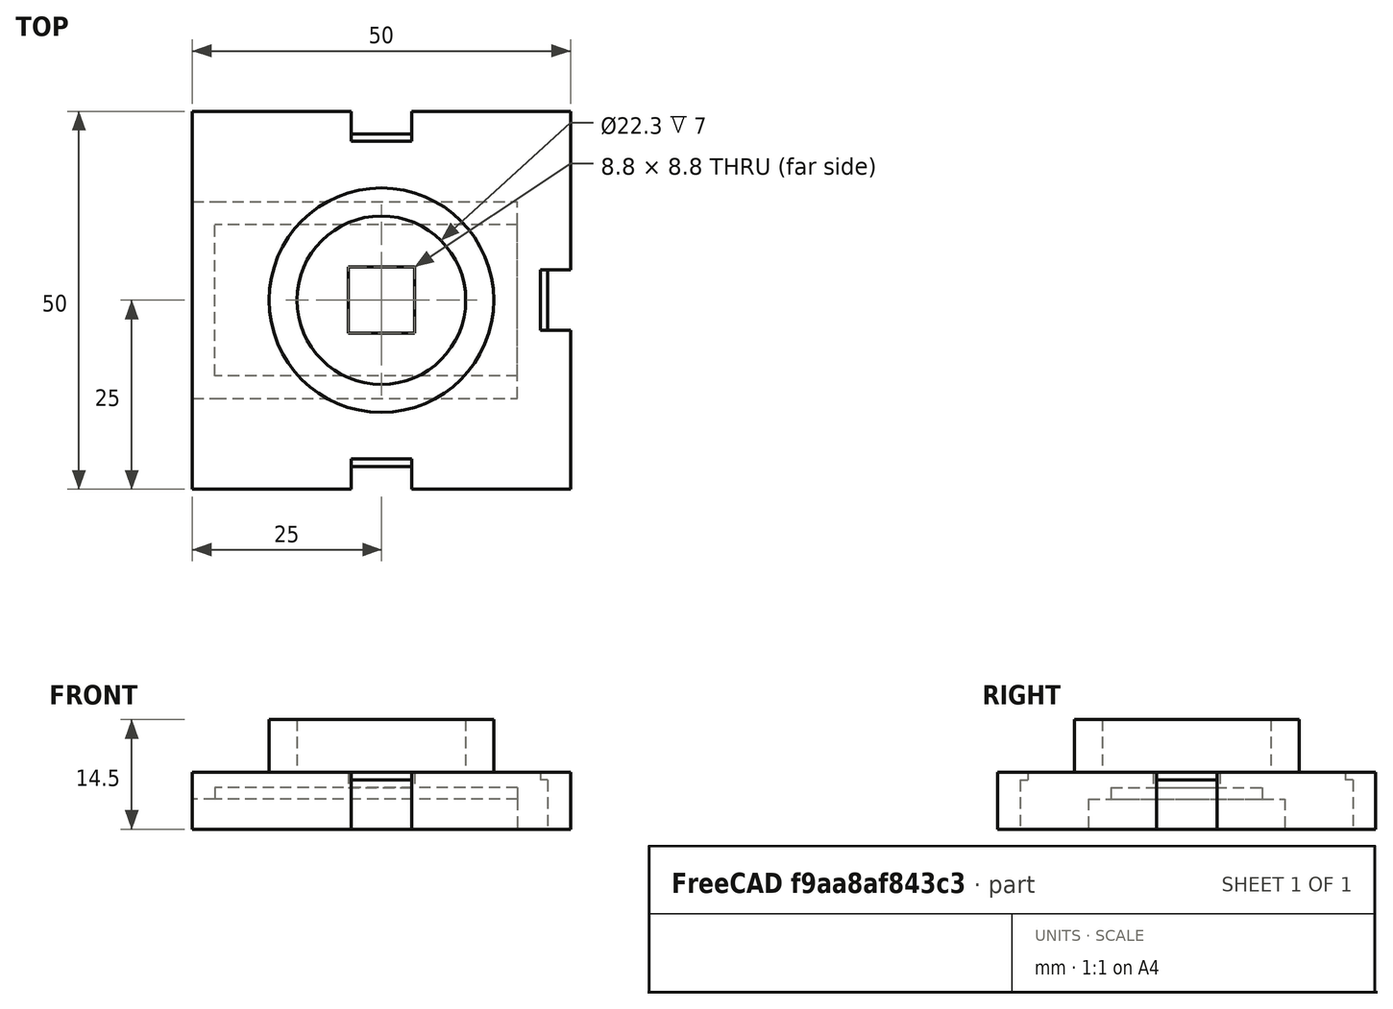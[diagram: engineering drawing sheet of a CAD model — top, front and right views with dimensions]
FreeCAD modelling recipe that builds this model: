
FCSTD DOCUMENT  (FreeCAD 0.16R6712 (Git))
Label: mount-125
License: All rights reserved
LicenseURL: http://en.wikipedia.org/wiki/All_rights_reserved
objects: Part::FeaturePython×13, Part::Box×10, Part::Cylinder×2
note: 25 computed .brp shape members not serialized (recipe doc carries the construction recipe); baked Part::Feature solids carry a one-line shape summary decoded from their .brp

FEATURE [Part::Box] Box  label="Base"
  Height = 7.5
  Length = 50
  Placement = pos=(-25,-25,0) rot=(0,0,1;0rad)
  Width = 50
FEATURE [Part::Box] Box001  label="立方体001"
  Height = 7
  Length = 40
  Placement = pos=(-18,-13,2) rot=(0,0,1;0rad)
  Width = 26
FEATURE [Part::FeaturePython] Cutout  # WARN: FeaturePython — macro-defined, semantics opaque (R4)
  Base = -> Box
  Mode = 3
  Tool = -> Box001
FEATURE [Part::Box] Box002  label="立方体"
  Height = 3
  Length = 8.8
  Placement = pos=(-4.4,-4.4,0) rot=(0,0,1;0rad)
  Width = 8.8
FEATURE [Part::FeaturePython] Cutout001  # WARN: FeaturePython — macro-defined, semantics opaque (R4)
  Base = -> Cutout
  Mode = 3
  Tool = -> Box002
FEATURE [Part::Box] Box003  label="立方体002"
  Height = 1.5
  Length = 41
  Placement = pos=(-18,10,2) rot=(0,0,1;0rad)
  Width = 4
FEATURE [Part::Box] Box004  label="立方体003"
  Height = 1.5
  Length = 41
  Placement = pos=(-18,-14,2) rot=(0,0,1;0rad)
  Width = 4
FEATURE [Part::FeaturePython] Connect  # WARN: FeaturePython — macro-defined, semantics opaque (R4)
  Base = -> Box003
  Mode = 1
  Tool = -> Cutout001
FEATURE [Part::FeaturePython] Connect001  # WARN: FeaturePython — macro-defined, semantics opaque (R4)
  Base = -> Box004
  Mode = 1
  Tool = -> Connect
FEATURE [Part::Box] Box005  label="立方体004"
  Height = 5.5
  Length = 3
  Placement = pos=(22,-13,3.5) rot=(0,0,1;0rad)
  Width = 26
FEATURE [Part::FeaturePython] Cutout002  # WARN: FeaturePython — macro-defined, semantics opaque (R4)
  Base = -> Connect001
  Mode = 3
  Tool = -> Box005
FEATURE [Part::Box] Box006  label="clip"
  Height = 9.5
  Length = 8
  Placement = pos=(-4,-32,-2) rot=(0,0,1;0rad)
  Width = 3
FEATURE [Part::Box] Box007  label="立方体005"
  Height = 3
  Length = 8
  Placement = pos=(-4,-30,-2) rot=(0,0,1;0rad)
  Width = 2
FEATURE [Part::FeaturePython] Connect002  label="Clip001"  # WARN: FeaturePython — macro-defined, semantics opaque (R4)
  Base = -> Box006
  Mode = 1
  Placement = pos=(0,7,0) rot=(0,0,1;0rad)
  Tool = -> Box007
FEATURE [Part::FeaturePython] Connect003  label="Clip002"  # WARN: FeaturePython — macro-defined, semantics opaque (R4)
  Base = -> Box006
  Mode = 1
  Placement = pos=(0,-7,0) rot=(0,0,1;3.14159rad)
  Tool = -> Box007
FEATURE [Part::Box] Box008  label="clip001"
  Height = 9.5
  Length = 8
  Placement = pos=(-4,-32,-2) rot=(0,0,1;0rad)
  Width = 3
FEATURE [Part::Box] Box009  label="立方体006"
  Height = 3
  Length = 8
  Placement = pos=(-4,-30,-2) rot=(0,0,1;0rad)
  Width = 2
FEATURE [Part::FeaturePython] Connect004  label="Clip003"  # WARN: FeaturePython — macro-defined, semantics opaque (R4)
  Base = -> Box008
  Mode = 1
  Placement = pos=(7,0,0) rot=(0,0,-1;1.5708rad)
  Tool = -> Box009
FEATURE [Part::FeaturePython] Cutout003  # WARN: FeaturePython — macro-defined, semantics opaque (R4)
  Base = -> Cutout002
  Mode = 3
  Tool = -> Connect002
FEATURE [Part::FeaturePython] Cutout004  # WARN: FeaturePython — macro-defined, semantics opaque (R4)
  Base = -> Cutout003
  Mode = 3
  Tool = -> Connect003
FEATURE [Part::FeaturePython] Cutout005  label="Holder"  # WARN: FeaturePython — macro-defined, semantics opaque (R4)
  Base = -> Cutout004
  Mode = 3
  Tool = -> Connect004
FEATURE [Part::Cylinder] Cylinder001  label="圆柱体001"
  Angle = 360
  Height = 7
  Placement = pos=(0,0,-5) rot=(0,0,1;0rad)
  Radius = 11.15
FEATURE [Part::Cylinder] Cylinder  label="圆柱体"
  Angle = 360
  Height = 7
  Placement = pos=(0,0,-5) rot=(0,0,1;0rad)
  Radius = 14.85
FEATURE [Part::FeaturePython] Cutout006  label="Connector"  # WARN: FeaturePython — macro-defined, semantics opaque (R4)
  Base = -> Cylinder
  Mode = 3
  Placement = pos=(0,0,-2) rot=(0,0,1;0rad)
  Tool = -> Cylinder001
FEATURE [Part::FeaturePython] Connect005  # WARN: FeaturePython — macro-defined, semantics opaque (R4)
  Base = -> Cutout005
  Mode = 1
  Placement = pos=(0,0,0) rot=(0,1,0;3.14159rad)
  Tool = -> Cutout006
